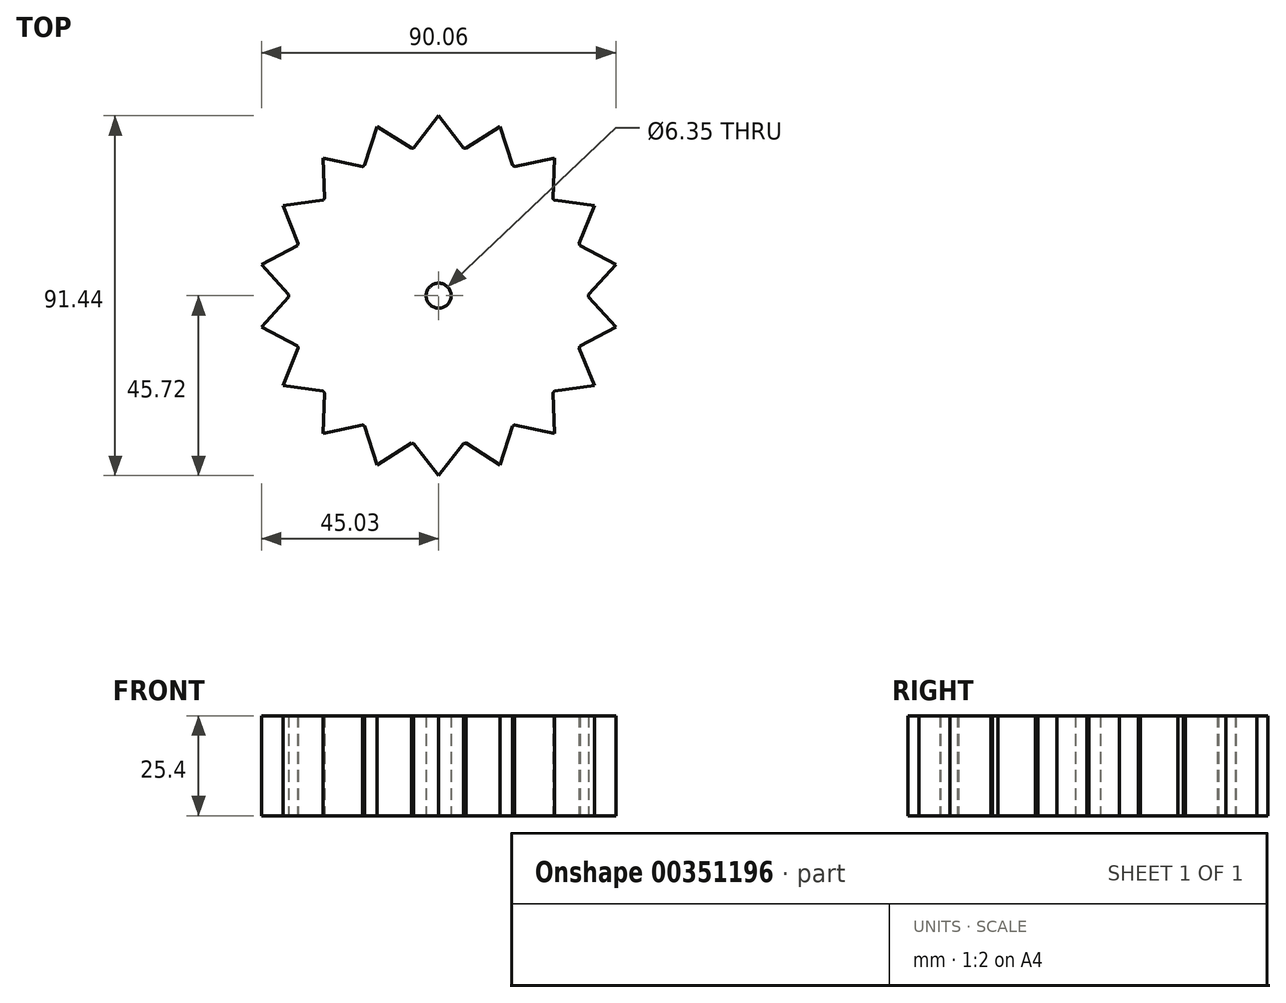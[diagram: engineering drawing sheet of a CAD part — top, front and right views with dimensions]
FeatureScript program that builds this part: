
annotation { "Feature Type Name" : "Feature", "Feature Type Description" : "" }
export const myFeature = defineFeature(function(context is Context, id is Id, definition is map)
    precondition{}
    {
        {
            var Q0;
            Q0=qCreatedBy(makeId("Top.planeOp"),FACE);
            var sketch = newSketch(context, id + "F0", { "sketchPlane" : qUnion([Q0])});
            skCircle(sketch, "E0", {"center": v(0, 0) * mm, "radius": 3.18 * mm});
            skArc(sketch, "E1", {"start": v(-6.33, 37.57) * mm, "mid": v(-6.62, 37.52) * mm, "end": v(-6.9, 37.47) * mm});
            skLineSegment(sketch, "E2", {"start": v(6.33, 37.57) * mm, "end": v(0, 45.72) * mm});
            skLineSegment(sketch, "E3", {"start": v(-6.33, 37.57) * mm, "end": v(0, 45.72) * mm});
            skLineSegment(sketch, "E4.1.0", {"start": v(-18.8, 33.14) * mm, "end": v(-15.64, 42.96) * mm});
            skLineSegment(sketch, "E4.1.1", {"start": v(-6.9, 37.47) * mm, "end": v(-15.64, 42.96) * mm});
            skLineSegment(sketch, "E4.2.0", {"start": v(-29, 24.71) * mm, "end": v(-29.39, 35.02) * mm});
            skLineSegment(sketch, "E4.2.1", {"start": v(-19.3, 32.85) * mm, "end": v(-29.39, 35.02) * mm});
            skLineSegment(sketch, "E4.3.0", {"start": v(-35.7, 13.3) * mm, "end": v(-39.6, 22.86) * mm});
            skLineSegment(sketch, "E4.3.1", {"start": v(-29.37, 24.27) * mm, "end": v(-39.6, 22.86) * mm});
            skLineSegment(sketch, "E4.4.0", {"start": v(-38.1, 0.3) * mm, "end": v(-45.03, 7.94) * mm});
            skLineSegment(sketch, "E4.4.1", {"start": v(-35.9, 12.76) * mm, "end": v(-45.03, 7.94) * mm});
            skLineSegment(sketch, "E4.5.0", {"start": v(-35.9, -12.76) * mm, "end": v(-45.03, -7.94) * mm});
            skLineSegment(sketch, "E4.5.1", {"start": v(-38.1, -0.3) * mm, "end": v(-45.03, -7.94) * mm});
            skLineSegment(sketch, "E4.6.0", {"start": v(-29.37, -24.27) * mm, "end": v(-39.6, -22.86) * mm});
            skLineSegment(sketch, "E4.6.1", {"start": v(-35.7, -13.3) * mm, "end": v(-39.6, -22.86) * mm});
            skLineSegment(sketch, "E4.7.0", {"start": v(-19.3, -32.85) * mm, "end": v(-29.39, -35.02) * mm});
            skLineSegment(sketch, "E4.7.1", {"start": v(-29, -24.71) * mm, "end": v(-29.39, -35.02) * mm});
            skLineSegment(sketch, "E4.8.0", {"start": v(-6.9, -37.47) * mm, "end": v(-15.64, -42.96) * mm});
            skLineSegment(sketch, "E4.8.1", {"start": v(-18.8, -33.14) * mm, "end": v(-15.64, -42.96) * mm});
            skLineSegment(sketch, "E4.9.0", {"start": v(6.33, -37.57) * mm, "end": v(0, -45.72) * mm});
            skLineSegment(sketch, "E4.9.1", {"start": v(-6.33, -37.57) * mm, "end": v(0, -45.72) * mm});
            skLineSegment(sketch, "E4.10.0", {"start": v(18.8, -33.14) * mm, "end": v(15.64, -42.96) * mm});
            skLineSegment(sketch, "E4.10.1", {"start": v(6.9, -37.47) * mm, "end": v(15.64, -42.96) * mm});
            skLineSegment(sketch, "E4.11.0", {"start": v(29, -24.71) * mm, "end": v(29.39, -35.02) * mm});
            skLineSegment(sketch, "E4.11.1", {"start": v(19.3, -32.85) * mm, "end": v(29.39, -35.02) * mm});
            skLineSegment(sketch, "E4.12.0", {"start": v(35.7, -13.3) * mm, "end": v(39.6, -22.86) * mm});
            skLineSegment(sketch, "E4.12.1", {"start": v(29.37, -24.27) * mm, "end": v(39.6, -22.86) * mm});
            skLineSegment(sketch, "E4.13.0", {"start": v(38.1, -0.3) * mm, "end": v(45.03, -7.94) * mm});
            skLineSegment(sketch, "E4.13.1", {"start": v(35.9, -12.76) * mm, "end": v(45.03, -7.94) * mm});
            skLineSegment(sketch, "E4.14.0", {"start": v(35.9, 12.76) * mm, "end": v(45.03, 7.94) * mm});
            skLineSegment(sketch, "E4.14.1", {"start": v(38.1, 0.3) * mm, "end": v(45.03, 7.94) * mm});
            skLineSegment(sketch, "E4.15.0", {"start": v(29.37, 24.27) * mm, "end": v(39.6, 22.86) * mm});
            skLineSegment(sketch, "E4.15.1", {"start": v(35.7, 13.3) * mm, "end": v(39.6, 22.86) * mm});
            skLineSegment(sketch, "E4.16.0", {"start": v(19.3, 32.85) * mm, "end": v(29.39, 35.02) * mm});
            skLineSegment(sketch, "E4.16.1", {"start": v(29, 24.71) * mm, "end": v(29.39, 35.02) * mm});
            skLineSegment(sketch, "E4.17.0", {"start": v(6.9, 37.47) * mm, "end": v(15.64, 42.96) * mm});
            skLineSegment(sketch, "E4.17.1", {"start": v(18.8, 33.14) * mm, "end": v(15.64, 42.96) * mm});
            skArc(sketch, "E5.trimOffspring", {"start": v(6.9, 37.47) * mm, "mid": v(6.62, 37.52) * mm, "end": v(6.33, 37.57) * mm});
            skArc(sketch, "E6.trimOffspring", {"start": v(19.3, 32.85) * mm, "mid": v(19.05, 33) * mm, "end": v(18.8, 33.14) * mm});
            skArc(sketch, "E7.trimOffspring", {"start": v(29.37, 24.27) * mm, "mid": v(29.19, 24.5) * mm, "end": v(29, 24.71) * mm});
            skArc(sketch, "E8.trimOffspring", {"start": v(35.9, 12.76) * mm, "mid": v(35.8, 13.03) * mm, "end": v(35.7, 13.3) * mm});
            skArc(sketch, "E9.trimOffspring", {"start": v(38.1, -0.3) * mm, "mid": v(38.1, 0) * mm, "end": v(38.1, 0.3) * mm});
            skArc(sketch, "E10.trimOffspring", {"start": v(35.7, -13.3) * mm, "mid": v(35.8, -13.03) * mm, "end": v(35.9, -12.76) * mm});
            skArc(sketch, "E11.trimOffspring", {"start": v(29, -24.71) * mm, "mid": v(29.19, -24.5) * mm, "end": v(29.37, -24.27) * mm});
            skArc(sketch, "E12.trimOffspring", {"start": v(18.8, -33.14) * mm, "mid": v(19.05, -33) * mm, "end": v(19.3, -32.85) * mm});
            skArc(sketch, "E13.trimOffspring", {"start": v(6.33, -37.57) * mm, "mid": v(6.62, -37.52) * mm, "end": v(6.9, -37.47) * mm});
            skArc(sketch, "E14.trimOffspring", {"start": v(-6.9, -37.47) * mm, "mid": v(-6.62, -37.52) * mm, "end": v(-6.33, -37.57) * mm});
            skArc(sketch, "E15.trimOffspring", {"start": v(-19.3, -32.85) * mm, "mid": v(-19.05, -33) * mm, "end": v(-18.8, -33.14) * mm});
            skArc(sketch, "E16.trimOffspring", {"start": v(-29.37, -24.27) * mm, "mid": v(-29.19, -24.5) * mm, "end": v(-29, -24.71) * mm});
            skArc(sketch, "E17.trimOffspring", {"start": v(-35.9, -12.76) * mm, "mid": v(-35.8, -13.03) * mm, "end": v(-35.7, -13.3) * mm});
            skArc(sketch, "E18.trimOffspring", {"start": v(-38.1, 0.3) * mm, "mid": v(-38.1, 0) * mm, "end": v(-38.1, -0.3) * mm});
            skArc(sketch, "E19.trimOffspring", {"start": v(-35.7, 13.3) * mm, "mid": v(-35.8, 13.03) * mm, "end": v(-35.9, 12.76) * mm});
            skArc(sketch, "E20.trimOffspring", {"start": v(-29, 24.71) * mm, "mid": v(-29.19, 24.5) * mm, "end": v(-29.37, 24.27) * mm});
            skArc(sketch, "E21.trimOffspring", {"start": v(-18.8, 33.14) * mm, "mid": v(-19.05, 33) * mm, "end": v(-19.3, 32.85) * mm});
            skSolve(sketch);
        }
        {
            var Q0;
            Q0=makeQuery(id+"F0.imprint","IMPRINT",FACE,{"disambiguationData":[TD([[makeQuery(id+"F0.imprint","IMPRINT",EDGE,{"derivedFrom":sQuery(id+"F0.wireOp",EDGE,"E0")}),-1.0]])]});
            extrude(context, id + "F1", {"entities" : qUnion([Q0]), "depth" : 25.4 * mm});
        }
    });
